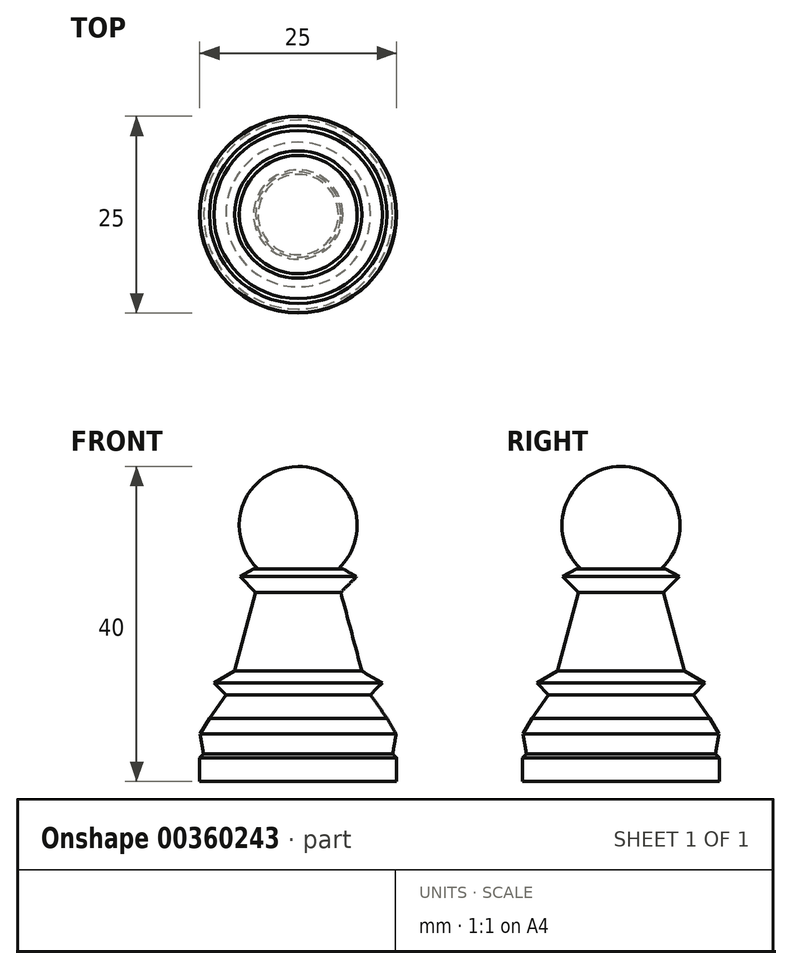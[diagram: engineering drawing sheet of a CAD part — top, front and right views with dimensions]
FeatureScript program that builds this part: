
annotation { "Feature Type Name" : "Feature", "Feature Type Description" : "" }
export const myFeature = defineFeature(function(context is Context, id is Id, definition is map)
    precondition{}
    {
        {
            var Q0;
            Q0=qCreatedBy(makeId("Top.planeOp"),FACE);
            var sketch = newSketch(context, id + "F0", { "sketchPlane" : qUnion([Q0])});
            skCircle(sketch, "E0", {"center": v(0, 0) * mm, "radius": 12.5 * mm});
            skSolve(sketch);
        }
        {
            var Q0;
            Q0=makeQuery(id+"F0.imprint","IMPRINT",FACE,{"disambiguationData":[TD([[makeQuery(id+"F0.imprint","IMPRINT",EDGE,{"derivedFrom":sQuery(id+"F0.wireOp",EDGE,"E0")}),1.0]])]});
            extrude(context, id + "F1", {"entities" : qUnion([Q0]), "depth" : 3 * mm});
        }
        {
            var Q0;
            Q0=makeQuery(id+"F1.opExtrude","CAP_FACE",FACE,{"disambiguationData":[OSD([sQuery(id+"F0.wireOp",EDGE,"E0")])],"isStart":false});
            extrude(context, id + "F2", {"entities" : qUnion([Q0]), "operationType" : NewBodyOperationType.ADD, "depth" : .5 * mm, "hasDraft" : true, "draftAngle" : 45 * degree, "draftPullDirection" : true});
        }
        {
            var Q0;
            Q0=makeQuery(id+"F2.opExtrude","CAP_FACE",FACE,{"disambiguationData":[OSD([sQuery(id+"F0.wireOp",EDGE,"E0")])],"isStart":false});
            extrude(context, id + "F3", {"entities" : qUnion([Q0]), "operationType" : NewBodyOperationType.ADD, "depth" : 2.5 * mm, "hasDraft" : true, "draftAngle" : 10 * degree});
        }
        {
            var Q0;
            Q0=makeQuery(id+"F3.opExtrude","CAP_FACE",FACE,{"disambiguationData":[OSD([sQuery(id+"F0.wireOp",EDGE,"E0")])],"isStart":false});
            extrude(context, id + "F4", {"entities" : qUnion([Q0]), "operationType" : NewBodyOperationType.ADD, "depth" : 2 * mm, "hasDraft" : true, "draftAngle" : 30 * degree, "draftPullDirection" : true});
        }
        {
            var Q0;
            Q0=makeQuery(id+"F4.opExtrude","CAP_FACE",FACE,{"disambiguationData":[OSD([sQuery(id+"F0.wireOp",EDGE,"E0")])],"isStart":false});
            extrude(context, id + "F5", {"entities" : qUnion([Q0]), "depth" : 3 * mm, "hasDraft" : true, "draftAngle" : 35 * degree, "draftPullDirection" : true});
        }
        {
            var Q0;
            Q0=makeQuery(id+"F5.opExtrude","CAP_FACE",FACE,{"disambiguationData":[OSD([sQuery(id+"F0.wireOp",EDGE,"E0")])],"isStart":false});
            extrude(context, id + "F6", {"entities" : qUnion([Q0]), "operationType" : NewBodyOperationType.ADD, "depth" : 1.5 * mm, "hasDraft" : true, "draftAngle" : 45 * degree});
        }
        {
            var Q0;
            Q0=makeQuery(id+"F6.opExtrude","CAP_FACE",FACE,{"disambiguationData":[OSD([sQuery(id+"F0.wireOp",EDGE,"E0")])],"isStart":false});
            extrude(context, id + "F7", {"entities" : qUnion([Q0]), "depth" : 1.5 * mm, "hasDraft" : true, "draftAngle" : 60 * degree, "draftPullDirection" : true});
        }
        {
            var Q0;
            Q0=makeQuery(id+"F7.opExtrude","CAP_FACE",FACE,{"disambiguationData":[OSD([sQuery(id+"F0.wireOp",EDGE,"E0")])],"isStart":false});
            extrude(context, id + "F8", {"entities" : qUnion([Q0]), "depth" : 10 * mm, "hasDraft" : true, "draftAngle" : 15 * degree, "draftPullDirection" : true});
        }
        {
            var Q0;
            Q0=makeQuery(id+"F8.opExtrude","CAP_FACE",FACE,{"disambiguationData":[OSD([sQuery(id+"F0.wireOp",EDGE,"E0")])],"isStart":false});
            extrude(context, id + "F9", {"entities" : qUnion([Q0]), "depth" : 2 * mm, "hasDraft" : true, "draftAngle" : 45 * degree});
        }
        {
            var Q0;
            Q0=makeQuery(id+"F9.opExtrude","CAP_FACE",FACE,{"disambiguationData":[OSD([sQuery(id+"F0.wireOp",EDGE,"E0")])],"isStart":false});
            extrude(context, id + "F10", {"entities" : qUnion([Q0]), "operationType" : NewBodyOperationType.ADD, "depth" : 1 * mm, "hasDraft" : true, "draftAngle" : 60 * degree, "draftPullDirection" : true});
        }
        {
            var Q0;
            Q0=qCreatedBy(makeId("Front.planeOp"),FACE);
            var sketch = newSketch(context, id + "F11", { "sketchPlane" : qUnion([Q0])});
            skLineSegment(sketch, "E1", {"start": v(0, 0) * mm, "end": v(0, 32.5) * mm});
            skCircle(sketch, "E2", {"center": v(0, 32.5) * mm, "radius": 7.5 * mm});
            skLineSegment(sketch, "E3", {"start": v(0, 32.5) * mm, "end": v(0, 43.46) * mm});
            skSolve(sketch);
        }
        {
            var Q0;
            {var subQ0=sQuery(id+"F11.wireOp",EDGE,"E3");var subQ1=sQuery(id+"F11.wireOp",EDGE,"E1");var subQ2=makeQuery(id+"F11.imprint","INTERSECT",VERTEX,{"derivedFrom":[subQ1,subQ0]});Q0=makeQuery(id+"F11.imprint","IMPRINT",FACE,{"disambiguationData":[TD([[makeQuery(id+"F11.imprint","IMPRINT",EDGE,{"disambiguationData":[TD([[subQ2,1.0]])],"derivedFrom":subQ1}),-1.0]])]});}
            var Q1;
            Q1=sQuery(id+"F11.wireOp",EDGE,"E3");
            revolve(context, id + "F12", {"operationType" : NewBodyOperationType.ADD, "entities" : qUnion([Q0]), "axis" : qUnion([Q1]), "revolveType" : RevolveType.FULL});
        }
    });
